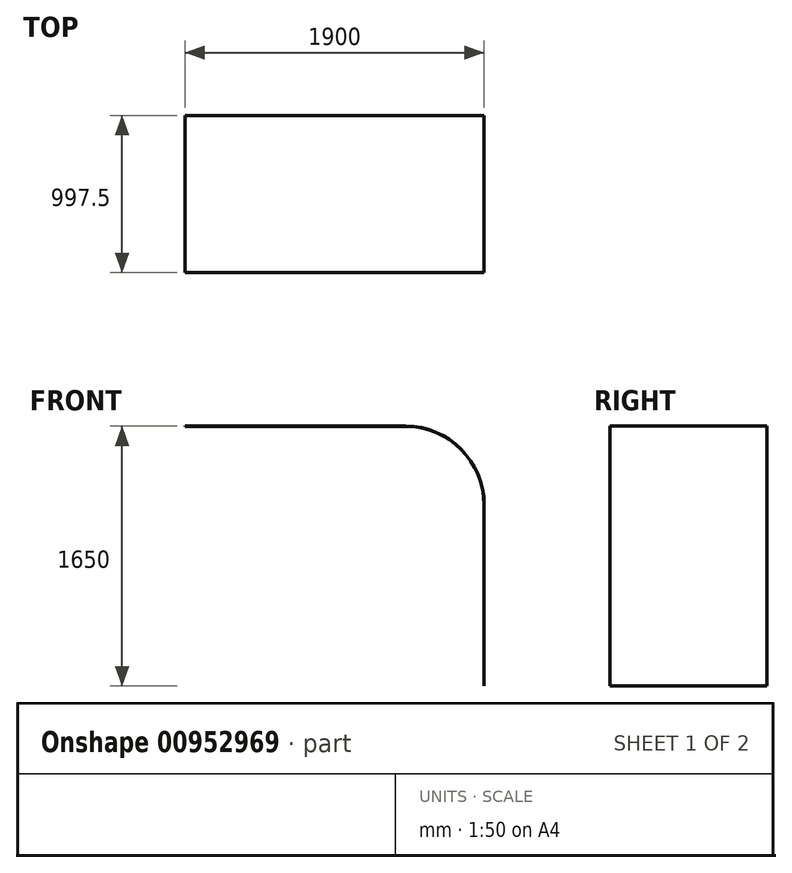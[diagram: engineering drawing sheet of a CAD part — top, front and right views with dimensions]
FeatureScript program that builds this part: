
annotation { "Feature Type Name" : "Feature", "Feature Type Description" : "" }
export const myFeature = defineFeature(function(context is Context, id is Id, definition is map)
    precondition{}
    {
        {
            var Q0;
            Q0=qCreatedBy(makeId("Front.planeOp"),FACE);
            var sketch = newSketch(context, id + "F0", { "sketchPlane" : qUnion([Q0])});
            skLineSegment(sketch, "E0", {"start": v(0, 0) * mm, "end": v(-700, 0) * mm});
            skLineSegment(sketch, "E1", {"start": v(-700, 0) * mm, "end": v(-700, 700) * mm});
            skLineSegment(sketch, "E2", {"start": v(-700, 700) * mm, "end": v(-950, 700) * mm});
            skCircle(sketch, "E3", {"center": v(-700, 700) * mm, "radius": 250 * mm});
            skLineSegment(sketch, "E4", {"start": v(-450, 700) * mm, "end": v(-450, 0) * mm});
            skLineSegment(sketch, "E5", {"start": v(-950, 700) * mm, "end": v(-950, 1650) * mm});
            skLineSegment(sketch, "E6", {"start": v(-950, 950) * mm, "end": v(-700, 950) * mm});
            skLineSegment(sketch, "E7", {"start": v(-450, 0) * mm, "end": v(250, 0) * mm});
            skLineSegment(sketch, "E8", {"start": v(250, 0) * mm, "end": v(250, 1150) * mm});
            skLineSegment(sketch, "E9", {"start": v(-950, 1650) * mm, "end": v(-250, 1650) * mm});
            skPoint(sketch, "E10.visualSharp", {"position": v(250, 1650) * mm});
            skArc(sketch, "E10.filletArc", {"start": v(250, 1150) * mm, "mid": v(103.55, 1503.55) * mm, "end": v(-250, 1650) * mm});
            skLineSegment(sketch, "E11", {"start": v(-950, 950) * mm, "end": v(-1650, 1650) * mm});
            skLineSegment(sketch, "E12", {"start": v(-950, 1650) * mm, "end": v(-1650, 1650) * mm});
            skArc(sketch, "E13", {"start": v(-450, 700) * mm, "mid": v(-523.22, 876.78) * mm, "end": v(-700, 950) * mm});
            skLineSegment(sketch, "E14.0", {"start": v(-950, 1648.75) * mm, "end": v(-1650, 1648.75) * mm});
            skLineSegment(sketch, "E14.1", {"start": v(-950, 1648.75) * mm, "end": v(-250, 1648.75) * mm});
            skArc(sketch, "E14.2", {"start": v(248.75, 1150) * mm, "mid": v(102.67, 1502.67) * mm, "end": v(-250, 1648.75) * mm});
            skLineSegment(sketch, "E14.3", {"start": v(248.75, 0) * mm, "end": v(248.75, 1150) * mm});
            skSolve(sketch);
        }
        {
            var Q0;
            {var subQ0=sQuery(id+"F0.wireOp",EDGE,"E12");Q0=makeQuery(id+"F0.imprint","IMPRINT",FACE,{"disambiguationData":[TD([[makeQuery(id+"F0.imprint","IMPRINT",EDGE,{"derivedFrom":subQ0}),1.0]])]});}
            var Q1;
            {var subQ0=sQuery(id+"F0.wireOp",EDGE,"E8");Q1=makeQuery(id+"F0.imprint","IMPRINT",FACE,{"disambiguationData":[TD([[makeQuery(id+"F0.imprint","IMPRINT",EDGE,{"derivedFrom":subQ0}),1.0]])]});}
            extrude(context, id + "F1", {"entities" : qUnion([Q0, Q1]), "depth" : (1000 - 2.5) * mm, "offsetDistance" : 25 * mm});
        }
    });
